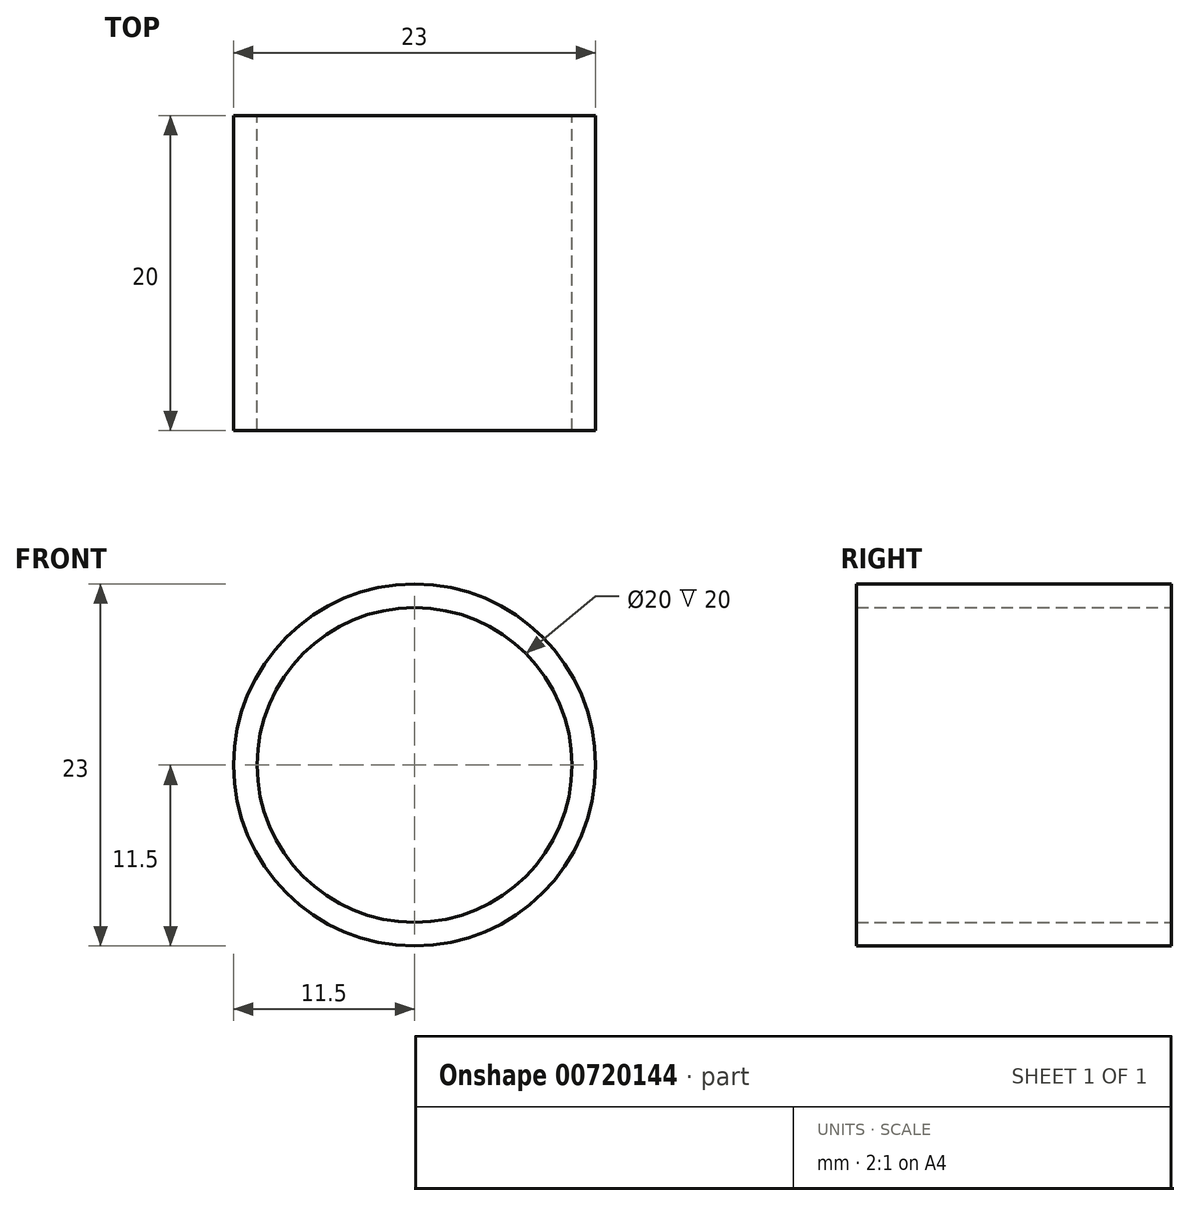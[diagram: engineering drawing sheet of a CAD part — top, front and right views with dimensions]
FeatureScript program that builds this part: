
annotation { "Feature Type Name" : "Feature", "Feature Type Description" : "" }
export const myFeature = defineFeature(function(context is Context, id is Id, definition is map)
    precondition{}
    {
        {
            var Q0;
            Q0=qCreatedBy(makeId("Front.planeOp"),FACE);
            var sketch = newSketch(context, id + "F0", { "sketchPlane" : qUnion([Q0])});
            skCircle(sketch, "E0", {"center": v(0, 0) * mm, "radius": 11.5 * mm});
            skCircle(sketch, "E1", {"center": v(0, 0) * mm, "radius": 10 * mm});
            skSolve(sketch);
        }
        {
            var Q0;
            Q0=makeQuery(id+"F0.imprint","IMPRINT",FACE,{"disambiguationData":[TD([[makeQuery(id+"F0.imprint","IMPRINT",EDGE,{"derivedFrom":sQuery(id+"F0.wireOp",EDGE,"E0")}),1.0]])]});
            extrude(context, id + "F1", {"entities" : qUnion([Q0]), "depth" : 20 * mm, "offsetDistance" : 25 * mm});
        }
    });
